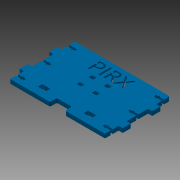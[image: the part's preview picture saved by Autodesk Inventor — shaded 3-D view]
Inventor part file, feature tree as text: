
AUTODESK INVENTOR PART (.ipt)
format: ipt  version: 2013 (Build 170138000, 138)  size: 430,592 bytes
history: native  units: mm
features: extrude x6, sketch x6, fillet x1
ambient origin geometry x8: Origin, YZ Plane, XZ Plane, XY Plane, X Axis, Y Axis, Z Axis, Center Point
bodies: Solid1 (feature_tree)
feature tree (13):
  extrude  "Extrusion1"  Depth=139.000017mm
  fillet  "Fillet1"  Radius=95.0mm
  extrude  "Extrusion9"  Depth=6.0mm
  extrude  "Extrusion10"  Depth=12.0mm
  extrude  "Extrusion5"  Depth=11.73562mm
  extrude  "Extrusion6"  Depth=1.8mm
  extrude  "Extrusion3"  Depth=1.25mm
  sketch  "Sketch1"  dims[d0=58.936344mm d2=139.000017mm d3=95.0mm]
  sketch  "Sketch3"  dims[d4=55.807226mm d5=6.0mm]
  sketch  "Sketch5"  dims[d6=2.0mm d7=12.0mm]
  sketch  "Sketch6"  dims[d8=12.0mm d9=11.73562mm]
  sketch  "Sketch9"  dims[d10=2.93562mm d11=1.8mm]
  sketch  "Sketch10"  dims[d12=3.0mm d13=1.25mm d14=1.25mm d15=8.5mm d16=3.0mm d17=1.25mm d18=1.25mm d19=8.5mm d20=19.9mm d21=0.1mm d22=11.8mm d23=46.0mm d24=3.0mm d25=1.25mm d26=1.25mm d27=19.9mm d28=6.4mm d29=5.0mm d30=6.4mm d31=5.0mm d32=12.6mm d33=16.0mm d34=30.099983mm d35=55.100017mm d36=11.803343mm d37=3.0mm d38=1.799994mm d39=6.0mm d40=22.0mm d41=10.0mm d42=58.5mm d44=6.0mm d45=0.0mm d48=2.0mm d49=69.5mm d50=86.4mm d51=203.2mm d52=10.0mm d53=0.0mm d56=10.0mm d57=0.0mm d58=6.0mm d59=0.0mm d77=10.0mm d78=0.0mm d79=2.3mm d81=6.0mm d82=0.0mm]
